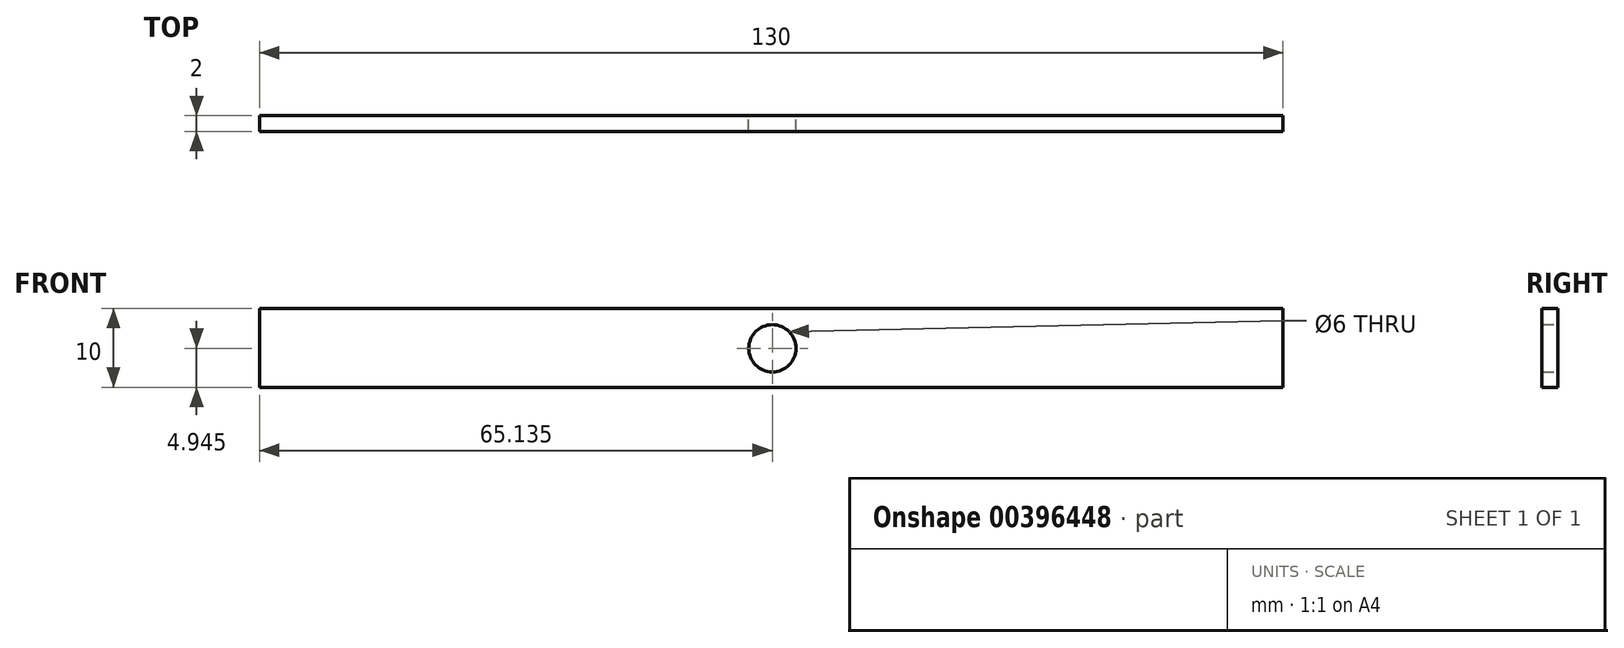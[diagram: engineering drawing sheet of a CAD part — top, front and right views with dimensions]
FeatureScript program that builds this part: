
annotation { "Feature Type Name" : "Feature", "Feature Type Description" : "" }
export const myFeature = defineFeature(function(context is Context, id is Id, definition is map)
    precondition{}
    {
        {
            var Q0;
            Q0=qCreatedBy(makeId("Front.planeOp"),FACE);
            var sketch = newSketch(context, id + "F0", { "sketchPlane" : qUnion([Q0])});
            skLineSegment(sketch, "E0.bottom", {"start": v(-93.73, 23.14) * mm, "end": v(36.27, 23.14) * mm});
            skLineSegment(sketch, "E0.top", {"start": v(-93.73, 13.14) * mm, "end": v(36.27, 13.14) * mm});
            skLineSegment(sketch, "E0.left", {"start": v(-93.73, 23.14) * mm, "end": v(-93.73, 13.14) * mm});
            skLineSegment(sketch, "E0.right", {"start": v(36.27, 23.14) * mm, "end": v(36.27, 13.14) * mm});
            skSolve(sketch);
        }
        {
            var Q0;
            Q0=makeQuery(id+"F0.imprint","IMPRINT",FACE,{"disambiguationData":[TD([[makeQuery(id+"F0.imprint","IMPRINT",EDGE,{"derivedFrom":sQuery(id+"F0.wireOp",EDGE,"E0.bottom")}),-1.0]])]});
            extrude(context, id + "F1", {"entities" : qUnion([Q0]), "depth" : 2 * mm});
        }
        {
            var Q0;
            Q0=makeQuery(id+"F1.opExtrude","CAP_FACE",FACE,{"disambiguationData":[OSD([sQuery(id+"F0.wireOp",EDGE,"E0.bottom"),sQuery(id+"F0.wireOp",EDGE,"E0.top"),sQuery(id+"F0.wireOp",EDGE,"E0.left"),sQuery(id+"F0.wireOp",EDGE,"E0.right")])],"isStart":true});
            var sketch = newSketch(context, id + "F2", { "sketchPlane" : qUnion([Q0])});
            skPoint(sketch, "E1", {"position": v(28.73, 13.14) * mm});
            skPoint(sketch, "E2", {"position": v(28.73, 23.14) * mm});
            skPoint(sketch, "E3", {"position": v(28.6, 18.09) * mm});
            skSolve(sketch);
        }
        {
            var Q0;
            Q0=sQuery(id+"F2.wireOp",VERTEX,"E3");
            var Q1;
            Q1=makeQuery(id+"F1.opExtrude","SWEPT_BODY",BODY,{"disambiguationData":[OSD([sQuery(id+"F0.wireOp",EDGE,"E0.bottom"),sQuery(id+"F0.wireOp",EDGE,"E0.top"),sQuery(id+"F0.wireOp",EDGE,"E0.left"),sQuery(id+"F0.wireOp",EDGE,"E0.right")])]});
            hole(context, id + "F3", {"style" : HoleStyle.SIMPLE, "endStyle" : HoleEndStyle.THROUGH, "holeDiameter" : 6 * mm, "isTappedThrough" : true, "tappedDepth" : 12 * mm, "tapClearance" : 3, "locations" : qUnion([Q0]), "scope" : qUnion([Q1])});
        }
    });
